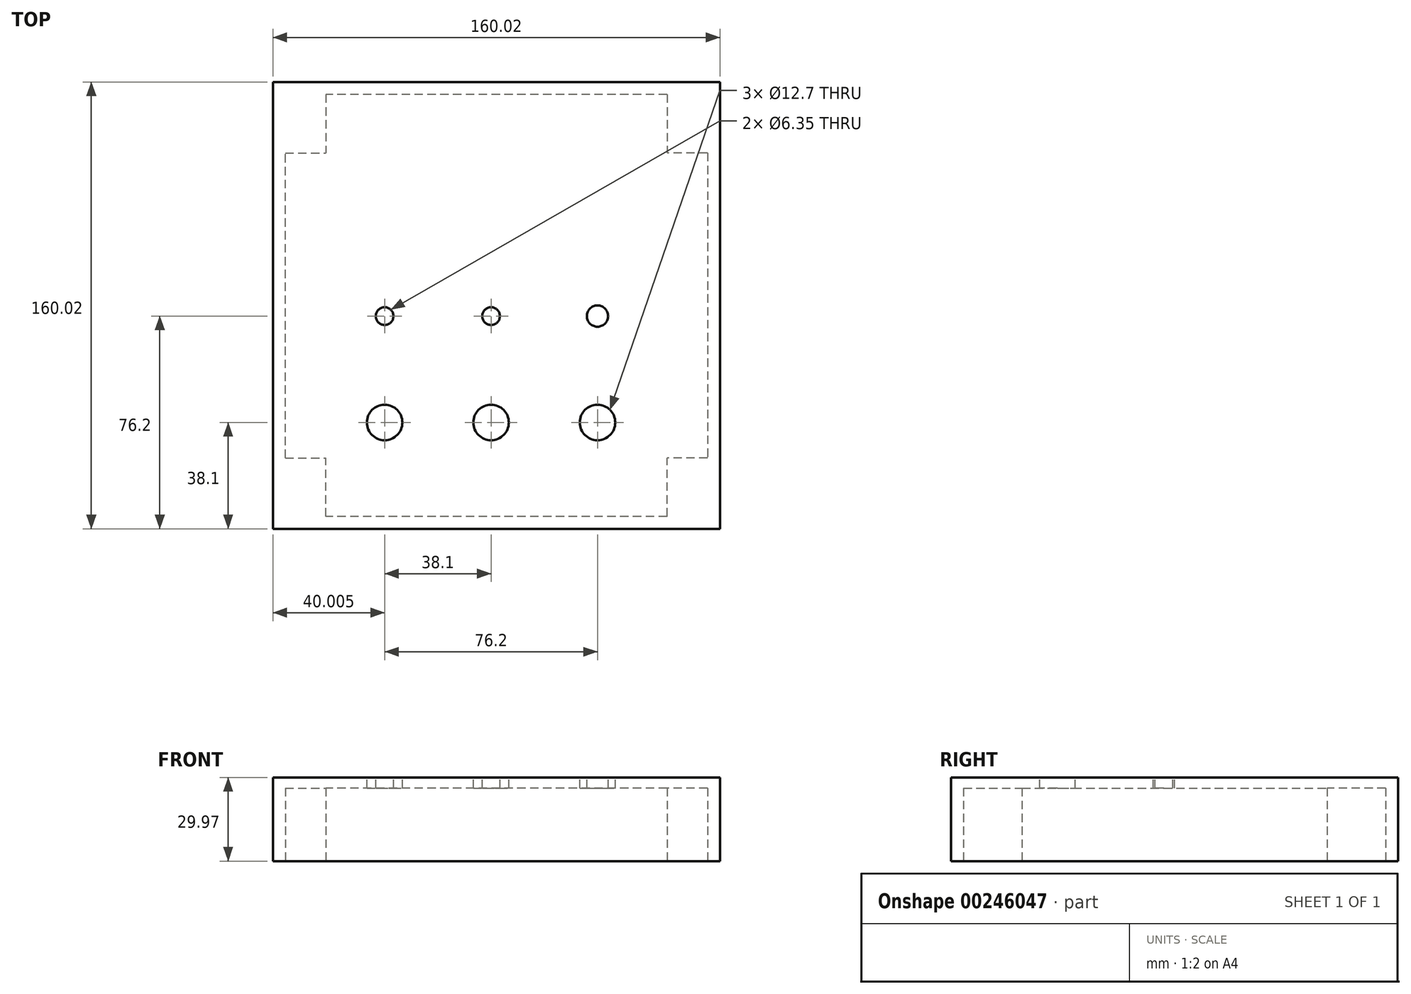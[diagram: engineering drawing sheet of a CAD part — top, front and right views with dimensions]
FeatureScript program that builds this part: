
annotation { "Feature Type Name" : "Feature", "Feature Type Description" : "" }
export const myFeature = defineFeature(function(context is Context, id is Id, definition is map)
    precondition{}
    {
        {
            var Q0;
            Q0=qCreatedBy(makeId("Top.planeOp"),FACE);
            var sketch = newSketch(context, id + "F0", { "sketchPlane" : qUnion([Q0])});
            skLineSegment(sketch, "E0.bottom", {"start": v(0, 0) * mm, "end": v(160.02, 0) * mm});
            skLineSegment(sketch, "E0.top", {"start": v(0, 160.02) * mm, "end": v(160.02, 160.02) * mm});
            skLineSegment(sketch, "E0.left", {"start": v(0, 0) * mm, "end": v(0, 160.02) * mm});
            skLineSegment(sketch, "E0.right", {"start": v(160.02, 0) * mm, "end": v(160.02, 160.02) * mm});
            skSolve(sketch);
        }
        {
            var Q0;
            Q0 = qSketchRegion(id + "F0", true);
            extrude(context, id + "F1", {"entities" : qUnion([Q0]), "oppositeDirection" : true, "depth" : 29.97 * mm});
        }
        {
            var Q0;
            Q0=makeQuery(id+"F1.opExtrude","CAP_FACE",FACE,{"disambiguationData":[OSD([sQuery(id+"F0.wireOp",EDGE,"E0.bottom"),sQuery(id+"F0.wireOp",EDGE,"E0.top"),sQuery(id+"F0.wireOp",EDGE,"E0.left"),sQuery(id+"F0.wireOp",EDGE,"E0.right")])],"isStart":false});
            var sketch = newSketch(context, id + "F2", { "sketchPlane" : qUnion([Q0])});
            skLineSegment(sketch, "E1.bottom", {"start": v(0, 0) * mm, "end": v(18.92, 0) * mm});
            skLineSegment(sketch, "E1.top", {"start": v(4.45, -25.4) * mm, "end": v(18.92, -25.4) * mm});
            skLineSegment(sketch, "E1.left", {"start": v(0, 0) * mm, "end": v(0, -25.4) * mm});
            skLineSegment(sketch, "E1.right", {"start": v(18.92, -4.45) * mm, "end": v(18.92, -25.4) * mm});
            skLineSegment(sketch, "E2.bottom", {"start": v(0, -160.02) * mm, "end": v(18.92, -160.02) * mm});
            skLineSegment(sketch, "E2.top", {"start": v(4.45, -134.62) * mm, "end": v(18.92, -134.62) * mm});
            skLineSegment(sketch, "E2.left", {"start": v(0, -160.02) * mm, "end": v(0, -134.62) * mm});
            skLineSegment(sketch, "E2.right", {"start": v(18.92, -155.58) * mm, "end": v(18.92, -134.62) * mm});
            skLineSegment(sketch, "E3.bottom", {"start": v(160.02, 0) * mm, "end": v(141.1, 0) * mm});
            skLineSegment(sketch, "E3.top", {"start": v(155.58, -25.4) * mm, "end": v(141.1, -25.4) * mm});
            skLineSegment(sketch, "E3.left", {"start": v(160.02, 0) * mm, "end": v(160.02, -25.4) * mm});
            skLineSegment(sketch, "E3.right", {"start": v(141.1, -4.45) * mm, "end": v(141.1, -25.4) * mm});
            skLineSegment(sketch, "E4.bottom", {"start": v(160.02, -160.02) * mm, "end": v(141.1, -160.02) * mm});
            skLineSegment(sketch, "E4.top", {"start": v(155.58, -134.62) * mm, "end": v(141.1, -134.62) * mm});
            skLineSegment(sketch, "E4.left", {"start": v(160.02, -160.02) * mm, "end": v(160.02, -134.62) * mm});
            skLineSegment(sketch, "E4.right", {"start": v(141.1, -155.58) * mm, "end": v(141.1, -134.62) * mm});
            skLineSegment(sketch, "E5.left", {"start": v(160.02, -134.62) * mm, "end": v(160.02, -25.4) * mm});
            skLineSegment(sketch, "E5.right", {"start": v(155.58, -134.62) * mm, "end": v(155.58, -25.4) * mm});
            skLineSegment(sketch, "E6.bottom", {"start": v(141.1, 0) * mm, "end": v(18.92, 0) * mm});
            skLineSegment(sketch, "E6.top", {"start": v(141.1, -4.45) * mm, "end": v(18.92, -4.45) * mm});
            skLineSegment(sketch, "E7.left", {"start": v(0, -25.4) * mm, "end": v(0, -134.62) * mm});
            skLineSegment(sketch, "E7.right", {"start": v(4.45, -25.4) * mm, "end": v(4.45, -134.62) * mm});
            skLineSegment(sketch, "E8.bottom", {"start": v(141.1, -160.02) * mm, "end": v(18.92, -160.02) * mm});
            skLineSegment(sketch, "E8.top", {"start": v(141.1, -155.58) * mm, "end": v(18.92, -155.58) * mm});
            skSolve(sketch);
        }
        {
            var Q0;
            Q0=makeQuery(id+"F2.imprint","IMPRINT",FACE,{"disambiguationData":[TD([[makeQuery(id+"F2.imprint","IMPRINT",EDGE,{"derivedFrom":sQuery(id+"F2.wireOp",EDGE,"E1.top")}),-1.0]])]});
            extrude(context, id + "F3", {"entities" : qUnion([Q0]), "operationType" : NewBodyOperationType.REMOVE, "oppositeDirection" : true, "depth" : 26.16 * mm});
        }
        {
            var Q0;
            Q0=makeQuery(id+"F1.opExtrude","CAP_FACE",FACE,{"disambiguationData":[OSD([sQuery(id+"F0.wireOp",EDGE,"E0.bottom"),sQuery(id+"F0.wireOp",EDGE,"E0.top"),sQuery(id+"F0.wireOp",EDGE,"E0.left"),sQuery(id+"F0.wireOp",EDGE,"E0.right")])],"isStart":true});
            var sketch = newSketch(context, id + "F4", { "sketchPlane" : qUnion([Q0])});
            skCircle(sketch, "E9", {"center": v(40, 38.1) * mm, "radius": 6.35 * mm});
            skCircle(sketch, "E10.1.0.0", {"center": v(78.1, 38.1) * mm, "radius": 6.35 * mm});
            skCircle(sketch, "E10.2.0.0", {"center": v(116.2, 38.1) * mm, "radius": 6.35 * mm});
            skLineSegment(sketch, "E10.direction1", {"start": v(40, 38.1) * mm, "end": v(78.1, 38.1) * mm, "construction": true});
            skCircle(sketch, "E11", {"center": v(40, 76.2) * mm, "radius": 3.18 * mm});
            skCircle(sketch, "E12.1.0.0", {"center": v(78.1, 76.2) * mm, "radius": 3.18 * mm});
            skLineSegment(sketch, "E12.direction1", {"start": v(40, 76.2) * mm, "end": v(78.1, 76.2) * mm, "construction": true});
            skCircle(sketch, "E13", {"center": v(116.2, 76.2) * mm, "radius": 3.81 * mm});
            skSolve(sketch);
        }
        {
            var Q0;
            Q0=makeQuery(id+"F4.imprint","IMPRINT",FACE,{"disambiguationData":[TD([[makeQuery(id+"F4.imprint","IMPRINT",EDGE,{"derivedFrom":sQuery(id+"F4.wireOp",EDGE,"E9")}),1.0]])]});
            var Q1;
            Q1=makeQuery(id+"F4.imprint","IMPRINT",FACE,{"disambiguationData":[TD([[makeQuery(id+"F4.imprint","IMPRINT",EDGE,{"derivedFrom":sQuery(id+"F4.wireOp",EDGE,"E10.1.0.0")}),1.0]])]});
            var Q2;
            Q2=makeQuery(id+"F4.imprint","IMPRINT",FACE,{"disambiguationData":[TD([[makeQuery(id+"F4.imprint","IMPRINT",EDGE,{"derivedFrom":sQuery(id+"F4.wireOp",EDGE,"E10.2.0.0")}),1.0]])]});
            var Q3;
            Q3=makeQuery(id+"F4.imprint","IMPRINT",FACE,{"disambiguationData":[TD([[makeQuery(id+"F4.imprint","IMPRINT",EDGE,{"derivedFrom":sQuery(id+"F4.wireOp",EDGE,"E13")}),1.0]])]});
            var Q4;
            Q4=makeQuery(id+"F4.imprint","IMPRINT",FACE,{"disambiguationData":[TD([[makeQuery(id+"F4.imprint","IMPRINT",EDGE,{"derivedFrom":sQuery(id+"F4.wireOp",EDGE,"E12.1.0.0")}),1.0]])]});
            var Q5;
            Q5=makeQuery(id+"F4.imprint","IMPRINT",FACE,{"disambiguationData":[TD([[makeQuery(id+"F4.imprint","IMPRINT",EDGE,{"derivedFrom":sQuery(id+"F4.wireOp",EDGE,"E11")}),1.0]])]});
            extrude(context, id + "F5", {"entities" : qUnion([Q0, Q1, Q2, Q3, Q4, Q5]), "operationType" : NewBodyOperationType.REMOVE, "oppositeDirection" : true, "depth" : 6.35 * mm});
        }
    });
